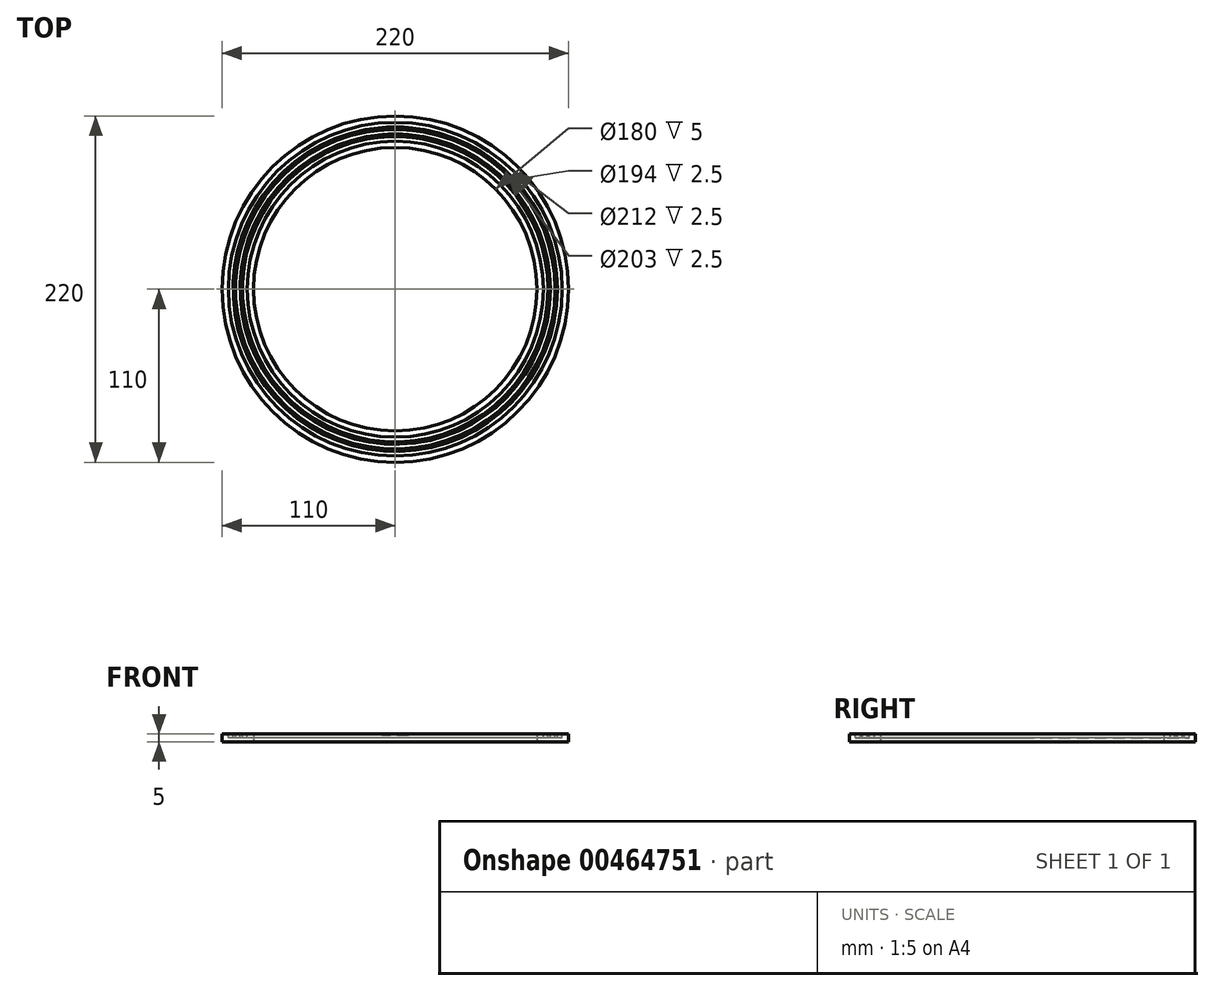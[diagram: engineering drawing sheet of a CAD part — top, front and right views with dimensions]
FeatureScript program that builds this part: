
annotation { "Feature Type Name" : "Feature", "Feature Type Description" : "" }
export const myFeature = defineFeature(function(context is Context, id is Id, definition is map)
    precondition{}
    {
        {
            var Q0;
            Q0=qCreatedBy(makeId("Top.planeOp"),FACE);
            var sketch = newSketch(context, id + "F0", { "sketchPlane" : qUnion([Q0])});
            skCircle(sketch, "E0", {"center": v(0, 0) * mm, "radius": 110 * mm});
            skCircle(sketch, "E1", {"center": v(0, 0) * mm, "radius": 90 * mm});
            skSolve(sketch);
        }
        {
            var Q0;
            Q0=makeQuery(id+"F0.imprint","IMPRINT",FACE,{"disambiguationData":[TD([[makeQuery(id+"F0.imprint","IMPRINT",EDGE,{"derivedFrom":sQuery(id+"F0.wireOp",EDGE,"E0")}),1.0]])]});
            extrude(context, id + "F1", {"entities" : qUnion([Q0]), "depth" : 5 * mm});
        }
        {
            var Q0;
            Q0=makeQuery(id+"F1.opExtrude","CAP_FACE",FACE,{"disambiguationData":[OSD([sQuery(id+"F0.wireOp",EDGE,"E0"),sQuery(id+"F0.wireOp",EDGE,"E1")])],"isStart":false});
            var sketch = newSketch(context, id + "F2", { "sketchPlane" : qUnion([Q0])});
            skLineSegment(sketch, "E2.bottom", {"start": v(-8.5, 105) * mm, "end": v(8.5, 105) * mm});
            skLineSegment(sketch, "E2.top", {"start": v(-8.5, 95) * mm, "end": v(8.5, 95) * mm});
            skLineSegment(sketch, "E2.left", {"start": v(-8.5, 105) * mm, "end": v(-8.5, 95) * mm});
            skLineSegment(sketch, "E2.right", {"start": v(8.5, 105) * mm, "end": v(8.5, 95) * mm});
            skCircle(sketch, "E3", {"center": v(0, 0) * mm, "radius": 100 * mm, "construction": true});
            skSolve(sketch);
        }
        {
            var Q0;
            Q0=makeQuery(id+"F1.opExtrude","CAP_FACE",FACE,{"disambiguationData":[OSD([sQuery(id+"F0.wireOp",EDGE,"E0"),sQuery(id+"F0.wireOp",EDGE,"E1")])],"isStart":false});
            var sketch = newSketch(context, id + "F3", { "sketchPlane" : qUnion([Q0])});
            skLineSegment(sketch, "E4", {"start": v(0, 0) * mm, "end": v(0, -124.39) * mm, "construction": true});
            skLineSegment(sketch, "E5", {"start": v(0, 0) * mm, "end": v(0, 128.62) * mm, "construction": true});
            skLineSegment(sketch, "E6", {"start": v(-17.32, 100) * mm, "end": v(17.32, 100) * mm, "construction": true});
            skCircle(sketch, "E7", {"center": v(0, 0) * mm, "radius": 100 * mm, "construction": true});
            skCircle(sketch, "E8", {"center": v(0, 0) * mm, "radius": 98.5 * mm});
            skCircle(sketch, "E9", {"center": v(0, 0) * mm, "radius": 101.5 * mm});
            skCircle(sketch, "E10", {"center": v(0, 0) * mm, "radius": 103 * mm});
            skCircle(sketch, "E11", {"center": v(0, 0) * mm, "radius": 106 * mm});
            skCircle(sketch, "E12", {"center": v(0, 0) * mm, "radius": 97 * mm});
            skCircle(sketch, "E13", {"center": v(0, 0) * mm, "radius": 94 * mm});
            skSolve(sketch);
        }
        {
            var Q0;
            Q0=makeQuery(id+"F2.imprint","IMPRINT",FACE,{"disambiguationData":[TD([[makeQuery(id+"F2.imprint","IMPRINT",EDGE,{"derivedFrom":sQuery(id+"F2.wireOp",EDGE,"E2.bottom")}),-1.0]])]});
            extrude(context, id + "F4", {"entities" : qUnion([Q0]), "operationType" : NewBodyOperationType.REMOVE, "oppositeDirection" : true, "depth" : 1 * mm});
        }
        {
            var Q0;
            Q0=makeQuery(id+"F3.imprint","IMPRINT",FACE,{"disambiguationData":[TD([[makeQuery(id+"F3.imprint","IMPRINT",EDGE,{"derivedFrom":sQuery(id+"F3.wireOp",EDGE,"E12")}),1.0]])]});
            var Q1;
            Q1=makeQuery(id+"F3.imprint","IMPRINT",FACE,{"disambiguationData":[TD([[makeQuery(id+"F3.imprint","IMPRINT",EDGE,{"derivedFrom":sQuery(id+"F3.wireOp",EDGE,"E8")}),-1.0]])]});
            var Q2;
            Q2=makeQuery(id+"F3.imprint","IMPRINT",FACE,{"disambiguationData":[TD([[makeQuery(id+"F3.imprint","IMPRINT",EDGE,{"derivedFrom":sQuery(id+"F3.wireOp",EDGE,"E10")}),-1.0]])]});
            extrude(context, id + "F5", {"entities" : qUnion([Q0, Q1, Q2]), "operationType" : NewBodyOperationType.REMOVE, "oppositeDirection" : true, "depth" : 2.5 * mm});
        }
        {
            var Q0;
            Q0=qCreatedBy(makeId("Front.planeOp"),FACE);
            var sketch = newSketch(context, id + "F6", { "sketchPlane" : qUnion([Q0])});
            skLineSegment(sketch, "E14", {"start": v(0, 0) * mm, "end": v(0, -50) * mm, "construction": true});
            skSolve(sketch);
        }
    });
